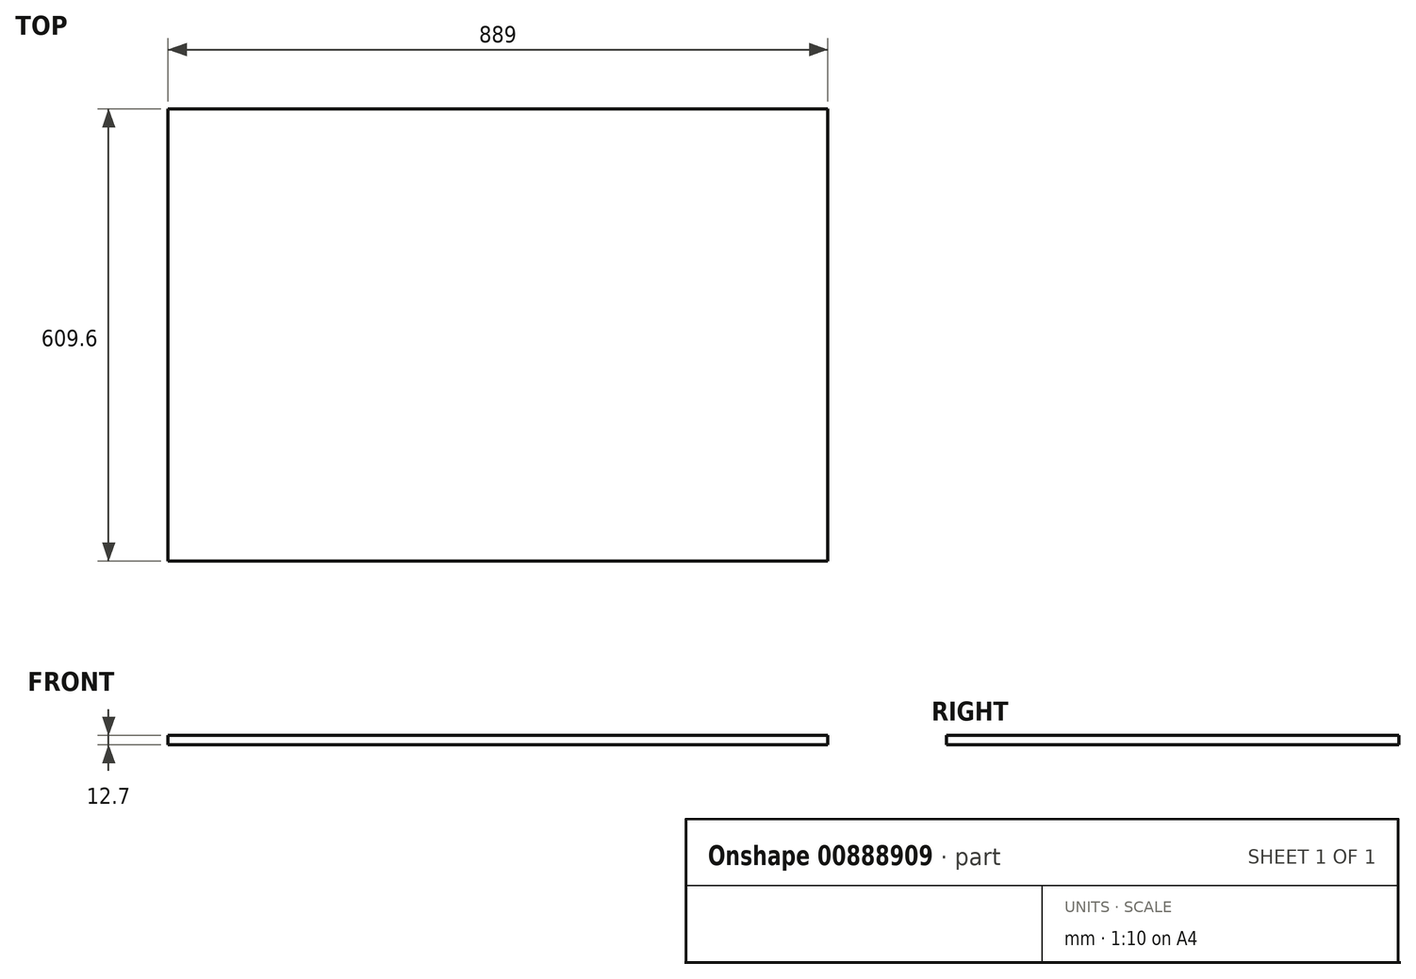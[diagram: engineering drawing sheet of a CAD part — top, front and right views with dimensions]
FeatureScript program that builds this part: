
annotation { "Feature Type Name" : "Feature", "Feature Type Description" : "" }
export const myFeature = defineFeature(function(context is Context, id is Id, definition is map)
    precondition{}
    {
        {
            var Q0;
            Q0=qCreatedBy(makeId("Top.planeOp"),FACE);
            var sketch = newSketch(context, id + "F0", { "sketchPlane" : qUnion([Q0])});
            skLineSegment(sketch, "E0.bottom", {"start": v(0, 0) * mm, "end": v(889, 0) * mm});
            skLineSegment(sketch, "E0.top", {"start": v(0, 609.6) * mm, "end": v(889, 609.6) * mm});
            skLineSegment(sketch, "E0.left", {"start": v(0, 0) * mm, "end": v(0, 609.6) * mm});
            skLineSegment(sketch, "E0.right", {"start": v(889, 0) * mm, "end": v(889, 609.6) * mm});
            skSolve(sketch);
        }
        {
            var Q0;
            Q0=makeQuery(id+"F0.imprint","IMPRINT",FACE,{"disambiguationData":[TD([[makeQuery(id+"F0.imprint","IMPRINT",EDGE,{"derivedFrom":sQuery(id+"F0.wireOp",EDGE,"E0.bottom")}),1.0]])]});
            extrude(context, id + "F1", {"entities" : qUnion([Q0]), "depth" : 12.7 * mm, "offsetDistance" : 25.4 * mm});
        }
    });
